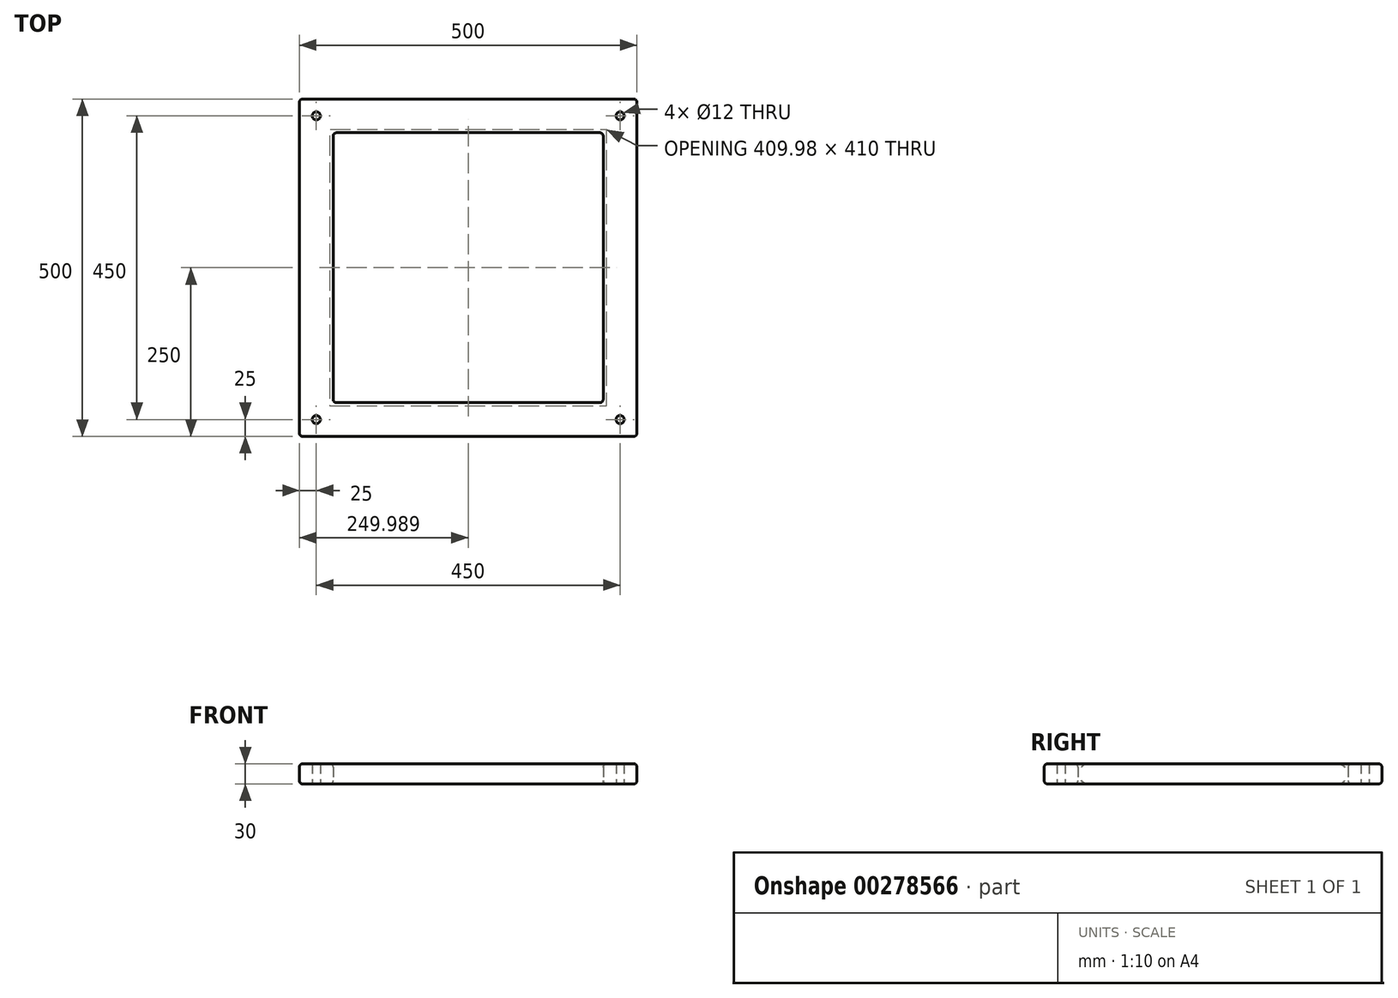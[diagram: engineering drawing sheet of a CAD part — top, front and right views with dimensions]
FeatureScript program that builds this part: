
annotation { "Feature Type Name" : "Feature", "Feature Type Description" : "" }
export const myFeature = defineFeature(function(context is Context, id is Id, definition is map)
    precondition{}
    {
        {
            var Q0;
            Q0=qCreatedBy(makeId("Top.planeOp"),FACE);
            var sketch = newSketch(context, id + "F0", { "sketchPlane" : qUnion([Q0])});
            skLineSegment(sketch, "E0", {"start": v(-446.99, 0) * mm, "end": v(406.86, 0) * mm, "construction": true});
            skLineSegment(sketch, "E1", {"start": v(0, 330.22) * mm, "end": v(0, -393.37) * mm, "construction": true});
            skLineSegment(sketch, "E2.bottom", {"start": v(250, 250) * mm, "end": v(-250, 250) * mm});
            skLineSegment(sketch, "E2.top", {"start": v(250, -250) * mm, "end": v(-250, -250) * mm});
            skLineSegment(sketch, "E2.left", {"start": v(250, 250) * mm, "end": v(250, -250) * mm});
            skLineSegment(sketch, "E2.right", {"start": v(-250, 250) * mm, "end": v(-250, -250) * mm});
            skPoint(sketch, "E2.middle", {"position": v(0, 0) * mm});
            skLineSegment(sketch, "E3.bottom", {"start": v(225, 225) * mm, "end": v(-225, 225) * mm, "construction": true});
            skLineSegment(sketch, "E3.top", {"start": v(225, -225) * mm, "end": v(-225, -225) * mm, "construction": true});
            skLineSegment(sketch, "E3.left", {"start": v(225, 225) * mm, "end": v(225, -225) * mm, "construction": true});
            skLineSegment(sketch, "E3.right", {"start": v(-225, 225) * mm, "end": v(-225, -225) * mm, "construction": true});
            skLineSegment(sketch, "E4.bottom", {"start": v(200, 200) * mm, "end": v(-200, 200) * mm});
            skLineSegment(sketch, "E4.top", {"start": v(200, -200) * mm, "end": v(-200, -200) * mm});
            skLineSegment(sketch, "E4.left", {"start": v(200, 200) * mm, "end": v(200, -200) * mm});
            skLineSegment(sketch, "E4.right", {"start": v(-200, 200) * mm, "end": v(-200, -200) * mm});
            skCircle(sketch, "E5", {"center": v(-225, 225) * mm, "radius": 6 * mm});
            skCircle(sketch, "E6.0.1.0", {"center": v(-225, -225) * mm, "radius": 6 * mm});
            skCircle(sketch, "E6.1.0.0", {"center": v(225, 225) * mm, "radius": 6 * mm});
            skCircle(sketch, "E6.1.1.0", {"center": v(225, -225) * mm, "radius": 6 * mm});
            skLineSegment(sketch, "E6.direction1", {"start": v(-225, 225) * mm, "end": v(225, 225) * mm, "construction": true});
            skSolve(sketch);
        }
        {
            var Q0;
            Q0=makeQuery(id+"F0.imprint","IMPRINT",FACE,{"disambiguationData":[TD([[makeQuery(id+"F0.imprint","IMPRINT",EDGE,{"derivedFrom":sQuery(id+"F0.wireOp",EDGE,"E2.bottom")}),1.0]])]});
            extrude(context, id + "F1", {"entities" : qUnion([Q0]), "depth" : 30 * mm});
        }
        {
            var Q0;
            Q0=makeQuery(id+"F1.opExtrude","SWEPT_FACE",FACE,{"disambiguationData":[OSD([sQuery(id+"F0.wireOp",EDGE,"E2.left")])]});
            var Q1;
            Q1=makeQuery(id+"F1.opExtrude","SWEPT_FACE",FACE,{"disambiguationData":[OSD([sQuery(id+"F0.wireOp",EDGE,"E2.bottom")])]});
            var Q2;
            Q2=makeQuery(id+"F1.opExtrude","CAP_EDGE",EDGE,{"disambiguationData":[OSD([sQuery(id+"F0.wireOp",EDGE,"E2.right")])],"isStart":false});
            var Q3;
            Q3=makeQuery(id+"F1.opExtrude","SWEPT_FACE",FACE,{"disambiguationData":[OSD([sQuery(id+"F0.wireOp",EDGE,"E2.right")])]});
            var Q4;
            Q4=makeQuery(id+"F1.opExtrude","SWEPT_FACE",FACE,{"disambiguationData":[OSD([sQuery(id+"F0.wireOp",EDGE,"E2.top")])]});
            var Q5;
            Q5=makeQuery(id+"F1.opExtrude","SWEPT_FACE",FACE,{"disambiguationData":[OSD([sQuery(id+"F0.wireOp",EDGE,"E4.right")])]});
            var Q6;
            Q6=makeQuery(id+"F1.opExtrude","SWEPT_FACE",FACE,{"disambiguationData":[OSD([sQuery(id+"F0.wireOp",EDGE,"E4.bottom")])]});
            var Q7;
            Q7=makeQuery(id+"F1.opExtrude","SWEPT_FACE",FACE,{"disambiguationData":[OSD([sQuery(id+"F0.wireOp",EDGE,"E4.top")])]});
            fillet(context, id + "F6", {"entities" : qUnion([Q0, Q1, Q2, Q3, Q4, Q5, Q6, Q7]), "radius" : 5 * mm, "tangentPropagation" : true, "allowEdgeOverflow" : false});
        }
        {
            var Q0;
            Q0=makeQuery(id+"F1.opExtrude","CAP_FACE",FACE,{"disambiguationData":[OSD([sQuery(id+"F0.wireOp",EDGE,"E2.bottom"),sQuery(id+"F0.wireOp",EDGE,"E2.top"),sQuery(id+"F0.wireOp",EDGE,"E2.left"),sQuery(id+"F0.wireOp",EDGE,"E2.right"),sQuery(id+"F0.wireOp",EDGE,"E4.bottom"),sQuery(id+"F0.wireOp",EDGE,"E4.top"),sQuery(id+"F0.wireOp",EDGE,"E4.left"),sQuery(id+"F0.wireOp",EDGE,"E4.right"),sQuery(id+"F0.wireOp",EDGE,"E5"),sQuery(id+"F0.wireOp",EDGE,"E6.0.1.0"),sQuery(id+"F0.wireOp",EDGE,"E6.1.0.0"),sQuery(id+"F0.wireOp",EDGE,"E6.1.1.0")])],"isStart":false});
            var sketch = newSketch(context, id + "F2", { "sketchPlane" : qUnion([Q0])});
            skPoint(sketch, "E7", {"position": v(225, 225) * mm});
            skSolve(sketch);
        }
        {
            var Q0;
            Q0=sQuery(id+"F2.wireOp",VERTEX,"E7");
            var Q1;
            Q1=sQuery(id+"F0.wireOp",VERTEX,"E6.1.0.0.center");
            var Q2;
            Q2=sQuery(id+"F0.wireOp",VERTEX,"E3.right.end");
            cPlane(context, id + "F7", {"entities" : qUnion([Q0, Q1, Q2]), "cplaneType" : CPlaneType.THREE_POINT, "offset" : 25 * mm, "width" : 150 * mm, "height" : 150 * mm});
        }
    });
